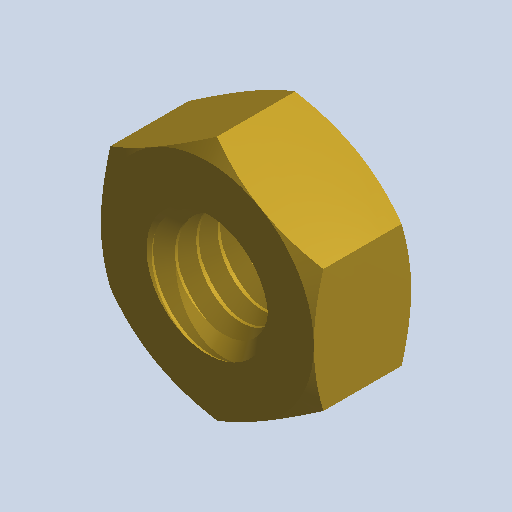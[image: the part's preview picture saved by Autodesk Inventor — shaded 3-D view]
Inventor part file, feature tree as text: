
AUTODESK INVENTOR PART (.ipt)
format: ipt  version: 2022.1 (Build 261234000, 234)  size: 230,912 bytes
history: native  units: mm (DEFAULTED — no unit token found)
features: other x8, mirror x1
bodies: Body1 (feature_tree)
feature tree (9):
  other  "Sólido1"
  other  "Origen"
  other  "Plano YZ"
  other  "Plano XZ"
  other  "Plano XY"
  other  "Eje X"
  other  "Eje Y"
  other  "Eje Z"
  mirror  "Mirror2"
